# Revit family: Trane_TVR_Indoor_High static pressure_4TVA0024(27,30,38)EF000AA(2nd DC)
name_source: partatom
category: Equipamento mecânico
units: mm (PartAtom-declared; Revit-internal decimal feet)

## family parameters
Com base no plano de trabalho = Não
Compartilhado = Não
Corte com vazios quando carregada = Não
Cota do conector redondo = Utilizar diâmetro
Número OmniClass = 23.75.00.00
Ponto de cálculo do ambiente = Não
Sempre na vertical = Sim
Tipo de parte = Normal
Título OmniClass = Climate Control (HVAC)

## types (4) — shared parameters
Condensation = air
Depth = 690
Descrição = High efficiency air cooled
Drain pipe = 25  [stored 0.082021 ft]
Fabricante = Trane
Gas = R410a
Gas pipe = 19.1  [stored 0.062664 ft]
Height = 423  [stored 1.3878 ft]
Installation = Indoor installation
Liquid pipe = 9.53
Machine material = grilles：ABS/HIPS
Maximum Fuse Amps = 15.000 A
Minimum Circuit Amps = 3.625 A
Power supply = 220-240V ~50/60Hz
Series = TVR ULTRA
URL = https://www.trane.com
Width = 965  [stored 3.16601 ft]
clearance access left = 500  [stored 1.64042 ft]
clearance access right = 600
zero-valued in all types: clearance access behind, clearance access front

## per-type parameters (varying)
| type | Air Flow | Cooling Capacity | Cooling Power Input | Heating Capacity | Heating Power Input | Net Weight |
| 4TVA0038EF000AA | 1870/1793/1697/1610/1523/1437/1350 | 11 kW | 380 W | 13 kW | 380 W | 48.00 kg |
| 4TVA0024EF000AA | 1360/1327/1293/1260/1227/1193/1160 | 7 kW | 180 W | 8 kW | 180 W | 41.00 kg |
| 4TVA0027EF000AA | 1360/1327/1293/1260/1227/1193/1160 | 8 kW | 180 W | 9 kW | 180 W | 41.00 kg |
| 4TVA0030EF000AA | 1420/1373/1327/1280/1233/1187/1140 | 9 kW | 220 W | 10 kW | 220 W | 48.00 kg |

note: column(s) folded — value = type name in every type: Modelo

note: [stored X ft] marks values corroborated as IEEE doubles in the binary element streams (Revit-internal decimal feet)

## geometry (parser evidence)
native form markers: Blend x2, Sweep x4
no freeform markers — native parametric forms only
